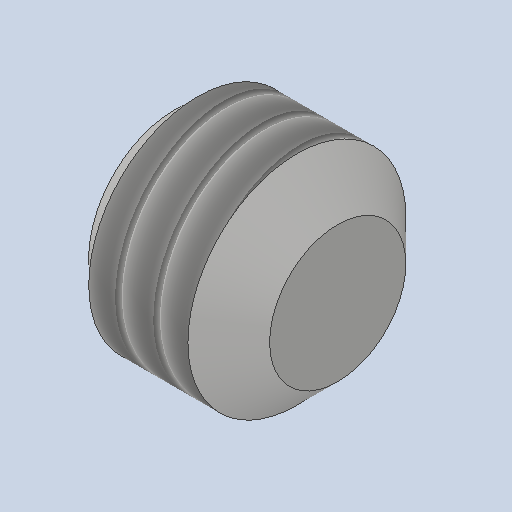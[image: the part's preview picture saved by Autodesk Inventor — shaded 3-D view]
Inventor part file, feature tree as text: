
AUTODESK INVENTOR PART (.ipt)
format: ipt  version: 2023 (Build 270158000, 158)  size: 171,520 bytes
history: native  units: mm
features: other x7, sketch x3, revolve x2, thread x1, extrude x1
ambient origin geometry x8: Origin, YZ Plane, XZ Plane, XY Plane, X Axis, Y Axis, Z Axis, Center Point
bodies: Solid1 (feature_tree)
feature tree (14):
  revolve  "Revolution1"  [1 undecoded]
  thread  "Thread1"  [1 undecoded]
  extrude  "Extrusion1"  TaperAngle=0.0deg  [1 undecoded]
  revolve  "Revolution2"  [1 undecoded]
  other  "CP_XY"
  other  "CP_YZ"
  other  "CP_ZX"
  other  "CP_X"
  other  "CP_Y"
  other  "CP_Z"
  other  "CP_Center"
  sketch  "Sketch_1"  dims[d0=360.0deg d1=1.8205mm d2=0.0mm d3=1.5mm d4=0.0mm]
  sketch  "Sketch_2"  dims[d5=360.0deg d6=0.0mm]
  sketch  "Sketch_3"
note: 4 required parameter values undecoded (feature->parameter linkage not recoverable at this tier; creation-order binding heuristic only, values carry confidence <= 0.55)